AUTODESK INVENTOR PART (.ipt)
format: ipt  version: unknown  size: 171,520 bytes
history: native  units: in
note: dims shown in document units (in); Inventor stores cm internally (conversion verified against a paired STEP export)
features: extrude x1, sketch x1
ambient origin geometry x8: Origin, YZ Plane, XZ Plane, XY Plane, X Axis, Y Axis, Z Axis, Center Point
bodies: Solid1 (feature_tree)
feature tree (2):
  extrude  "Extrusion1"  Depth=1.1811in
  sketch  "Sketch1"  dims[d0=1.0in d1=1.1811in d3=36.0in d4=1.1811in d6=36.0in d9=0.06in d10=0.0in]
